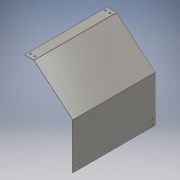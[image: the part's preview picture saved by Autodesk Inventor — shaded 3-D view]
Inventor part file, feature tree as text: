
AUTODESK INVENTOR PART (.ipt)
format: ipt  version: 2016 (Build 200138000, 138)  size: 210,944 bytes
history: native  units: mm
features: sheet_metal_op x10, sketch x6, other x5, hole x2
ambient origin geometry x8: Origin, YZ Plane, XZ Plane, XY Plane, X Axis, Y Axis, Z Axis, Center Point
bodies: Solid1 (feature_tree)
feature tree (23):
  sheet_metal_op  "Face1"
  sheet_metal_op  "Flange1"
  sheet_metal_op  "Flange2"
  sheet_metal_op  "Flange3"
  hole  "Hole1"  [1 undecoded]
  hole  "Hole2"  [1 undecoded]
  sketch  "Sketch1"  dims[d0=570.0mm d1=251.0mm]
  other  "Plate1"
  sketch  "Sketch2"  dims[d2=1.6mm d3=1.6mm]
  other  "Plate2"
  sheet_metal_op  "Bend1"
  sheet_metal_op  "Corner1"
  sketch  "Sketch3"  dims[d4=0.8mm]
  other  "Plate3"
  sheet_metal_op  "Bend2"
  sheet_metal_op  "Corner2"
  sketch  "Sketch4"  dims[d5=3.2mm]
  other  "Plate4"
  sheet_metal_op  "Bend3"
  sheet_metal_op  "Corner3"
  sketch  "Sketch5"  dims[d6=1.6mm]
  sketch  "Sketch6"  dims[d7=350.0mm d8=-8.726646mm d9=1.6mm d10=6.4mm d11=1.6mm d12=1.6mm d13=1.6mm d14=0.8mm d15=3.2mm d16=1.6mm d17=65.0mm d18=-6.981317mm d19=1.6mm d20=6.4mm d21=1.6mm d22=1.6mm d23=1.6mm d24=0.8mm d25=3.2mm d26=1.6mm d27=65.0mm d28=0.0mm d29=1.6mm d30=6.4mm d31=1.6mm d32=1.6mm d33=60.0mm d34=12.0mm d35=12.0mm d36=15.0mm d37=15.0mm d38=25.0mm d39=25.0mm d40=12.0mm d41=12.0mm d42=25.0mm d43=25.0mm d44=12.0mm d45=6.0mm d46=4.0mm d47=2.0mm d48=90.0deg d49=1.6mm d50=20.594885mm d51=60.0mm d52=12.0mm d53=12.0mm d54=25.0mm d55=25.0mm d56=15.0mm d57=15.0mm d58=12.0mm d59=12.0mm d60=25.0mm d61=25.0mm d62=12.0mm d63=6.0mm d64=4.0mm d65=2.0mm d66=90.0deg d67=1.6mm d68=20.594885mm]
  other  "Definition1"
note: 2 required parameter values undecoded (feature->parameter linkage not recoverable at this tier; creation-order binding heuristic only, values carry confidence <= 0.55)
